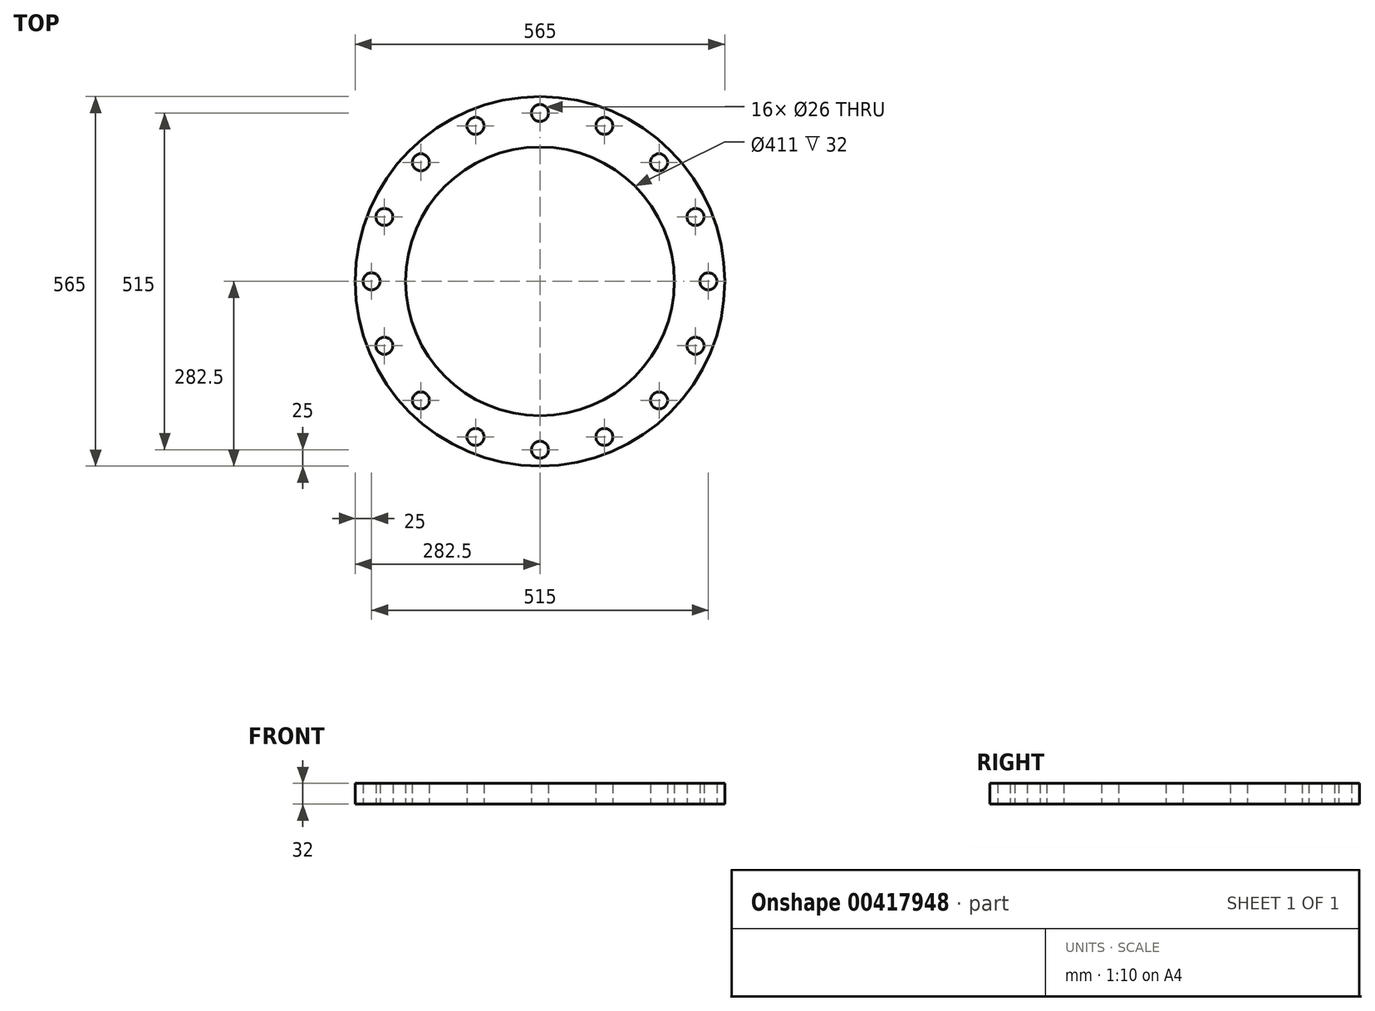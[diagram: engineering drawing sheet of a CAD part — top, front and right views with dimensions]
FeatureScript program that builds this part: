
annotation { "Feature Type Name" : "Feature", "Feature Type Description" : "" }
export const myFeature = defineFeature(function(context is Context, id is Id, definition is map)
    precondition{}
    {
        {
            var Q0;
            Q0=qCreatedBy(makeId("Top.planeOp"),FACE);
            var sketch = newSketch(context, id + "F0", { "sketchPlane" : qUnion([Q0])});
            skCircle(sketch, "E0", {"center": v(0, 0) * mm, "radius": 282.5 * mm});
            skCircle(sketch, "E1", {"center": v(0, 0) * mm, "radius": 205.5 * mm});
            skCircle(sketch, "E2", {"center": v(257.5, 0) * mm, "radius": 13 * mm});
            skCircle(sketch, "E3.1.0", {"center": v(237.9, 98.54) * mm, "radius": 13 * mm});
            skCircle(sketch, "E3.2.0", {"center": v(182.08, 182.08) * mm, "radius": 13 * mm});
            skCircle(sketch, "E3.3.0", {"center": v(98.54, 237.9) * mm, "radius": 13 * mm});
            skCircle(sketch, "E3.4.0", {"center": v(0, 257.5) * mm, "radius": 13 * mm});
            skCircle(sketch, "E3.5.0", {"center": v(-98.54, 237.9) * mm, "radius": 13 * mm});
            skCircle(sketch, "E3.6.0", {"center": v(-182.08, 182.08) * mm, "radius": 13 * mm});
            skCircle(sketch, "E3.7.0", {"center": v(-237.9, 98.54) * mm, "radius": 13 * mm});
            skCircle(sketch, "E3.8.0", {"center": v(-257.5, 0) * mm, "radius": 13 * mm});
            skCircle(sketch, "E3.9.0", {"center": v(-237.9, -98.54) * mm, "radius": 13 * mm});
            skCircle(sketch, "E3.10.0", {"center": v(-182.08, -182.08) * mm, "radius": 13 * mm});
            skCircle(sketch, "E3.11.0", {"center": v(-98.54, -237.9) * mm, "radius": 13 * mm});
            skCircle(sketch, "E3.12.0", {"center": v(0, -257.5) * mm, "radius": 13 * mm});
            skCircle(sketch, "E3.13.0", {"center": v(98.54, -237.9) * mm, "radius": 13 * mm});
            skCircle(sketch, "E3.14.0", {"center": v(182.08, -182.08) * mm, "radius": 13 * mm});
            skCircle(sketch, "E3.15.0", {"center": v(237.9, -98.54) * mm, "radius": 13 * mm});
            skSolve(sketch);
        }
        {
            var Q0;
            Q0=makeQuery(id+"F0.imprint","IMPRINT",FACE,{"disambiguationData":[TD([[makeQuery(id+"F0.imprint","IMPRINT",EDGE,{"derivedFrom":sQuery(id+"F0.wireOp",EDGE,"E0")}),1.0]])]});
            extrude(context, id + "F1", {"entities" : qUnion([Q0]), "depth" : 32 * mm});
        }
    });
